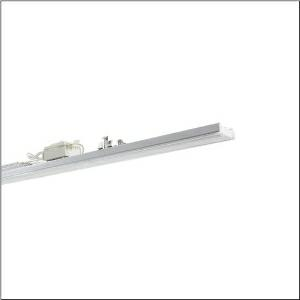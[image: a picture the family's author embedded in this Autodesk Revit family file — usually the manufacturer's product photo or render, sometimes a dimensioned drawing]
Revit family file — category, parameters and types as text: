
# Revit family: licross_r__21_recessed_mo_52tl18vn565g_8bae
name_source: partatom
category: Lighting Fixtures
units: mm (PartAtom-declared; Revit-internal decimal feet)

## family parameters
Cut with Voids When Loaded = No
Host = Face
Light Source = No
Part Type = Normal
Room Calculation Point = No
Round Connector Dimension = Use Diameter
Shared = No

## types (1)
- --- (1 x LED, 6500 lm, 37.3 W, 5000K)
    Apparent Load = 37 VA
    CIE Flux Codes = 79 95 99 100 100
    Color Rendering = 80
    Color Temperature = 5000K
    Default Elevation = 1800 mm
    Description = Licross® 21 Recessed MO, luminaire insert, of sheet steel, galvanised, coil coated, white, length: 1.500mm, width: 66mm, height: 67mm, LED rated luminous flux: 6.500lm, light colour: 850, control gear: DALI 2, CLO, with plug, 5-pole, with phase selection, mains connection: 220..240V, AC, 50/60Hz, start of lifetime: 37W, end of service life: 44W, internal wiring halogen-free, primary optical cover: cover, of PMMA, light emission: direct distribution, primary light characteristic: symmetric, protection rating (complete): IP40, insulation class (complete): insulation class I (protective earthing), certification: CE, ENEC, VDE, UKCA, protection symbol: D if used in an environment without relevant dust loads with corresponding accessories, impact resistance: IK06, permissible ambient temperature for indoor applications: -25..+40°C, corresponds to IFS (International Featured Standards) requirements for safety and quality in the food industry, reducing of maximum allowable ambient temperature of 5°C with ceiling mounting, LABS conformity tested according to VDMA 24364:2018-05, packaging unit: 1 piece
    Height = 58 mm
    Lamp = 1 x LED
    Lamp Light Flux = 6500 lm
    Lamp Power = 37.3 W
    Lamp count = 1
    Length = 1500 mm
    Luminous efficacy = 174 lm/W
    Manufacturer = Siteco
    ModVariant = No
    Model = 52TL18VN565G
    Mounting Place = Ceiling
    Mounting Type = Pendant
    Number of Poles = 1
    OnlyDefault = Yes
    Power Factor = 1
    Product Name = Licross® 21 Recessed MO
    Product group = luminaire insert | ceiling pendant
    ProductGroupID = 902
    Protection Class = Protection class I
    Protection Degree = IP 40
    RLX_Detail_Level = 1
    RLX_Emergency_Light_Flux = 0 lm
    RLX_Emergency_Type = 0
    RLX_Emergency_Type_DB = No
    RlxData = <blob elided: 24605 chars, md5=c6a43cc5>
    Socket = socket
    Standby Power = 0 W
    System Light Flux = 6500 lm
    System Power = 37 W
    Type Comments = factory setting: luminous flux: 100 % | dim-lin: 254 | 249 mA
    Type Image = l_1296930.jpg
    URL = http://relux.com
    VarID = @adj_103633
    Voltage = 0 V
    Weight = 0.00 kg
    Width = 66 mm

## geometry (parser evidence)
native form markers: Blend x4, Sweep x10
no freeform markers — native parametric forms only
